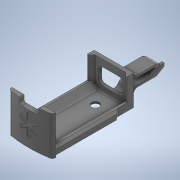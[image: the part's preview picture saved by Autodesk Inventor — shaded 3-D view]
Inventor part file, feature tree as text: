
AUTODESK INVENTOR PART (.ipt)
format: ipt  version: 2020 (Build 240168000, 168)  size: 811,008 bytes
history: native  units: mm
features: projected_geometry x32, extrude x18, sketch x16, fillet x10, other x9, chamfer x2
ambient origin geometry x8: Origin, YZ Plane, XZ Plane, XY Plane, X Axis, Y Axis, Z Axis, Center Point
bodies: Body1 (feature_tree)
feature tree (87):
  other  "Твердое тело1"
  sketch  "Эскиз1"
  extrude  "Выдавливание3"  Depth=202.0mm
  other  "РабПлоскость1"
  extrude  "Выдавливание1"  Depth=35.0mm
  other  "РабПлоскость2"
  sketch  "Эскиз2"
  extrude  "Выдавливание4"  Depth=68.0mm
  extrude  "Выдавливание5"  Depth=2.0mm
  sketch  "Эскиз4"
  extrude  "Выдавливание6"  Depth=2.0mm
  extrude  "Выдавливание7"  Depth=3.0mm
  other  "РабПлоскость3"
  extrude  "Выдавливание8"  Depth=3.0mm
  other  "РабПлоскость4"
  extrude  "Выдавливание9"  Depth=210.0mm
  sketch  "Эскиз8"
  extrude  "Выдавливание10"  Depth=20.0mm TaperAngle=0.0deg
  fillet  "Сопряжение1"  Radius=1.5mm
  fillet  "Сопряжение2"  Radius=28.0mm
  fillet  "Сопряжение3"  Radius=7.0mm
  fillet  "Сопряжение4"  Radius=20.0mm
  fillet  "Сопряжение5"  Radius=13.0mm
  extrude  "Выдавливание11"  Depth=5.0mm
  extrude  "Выдавливание12"  Depth=3.0mm
  fillet  "Сопряжение6"  Radius=10.0mm
  extrude  "Выдавливание13"  Depth=84.0mm
  chamfer  "Фаска1"  Distance=5.0mm
  fillet  "Сопряжение7"  Radius=52.0mm
  sketch  "Эскиз10"
  other  "РабПлоскость5"
  extrude  "Выдавливание14"  Depth=5.0mm TaperAngle=0.0deg
  fillet  "Сопряжение8"  Radius=35.0mm
  extrude  "Выдавливание15"  Depth=18.0mm
  fillet  "Сопряжение9"  Radius=3.0mm
  extrude  "Выдавливание16"  Depth=30.0mm TaperAngle=360.0deg
  fillet  "Сопряжение10"  Radius=0.5mm
  extrude  "Выдавливание17"  TaperAngle=0.0deg  [1 undecoded]
  chamfer  "Фаска2"  Distance=8.0mm
  other  "РабПлоскость10"
  other  "РабПлоскость9"
  sketch  "Эскиз14"
  other  "РабПлоскость8"
  sketch  "Эскиз15"
  sketch  "Эскиз16"
  sketch  "Эскиз17"
  extrude  "Выдавливание20"  Depth=2.0mm
  extrude  "Выдавливание21"  Depth=1.5mm TaperAngle=0.0deg
  projected_geometry  "Спроецированная петля1"
  projected_geometry  "Спроецированная петля7"
  projected_geometry  "Спроецированная петля8"
  sketch  "Эскиз3"
  projected_geometry  "Спроецированная петля9"
  projected_geometry  "Спроецированная петля10"
  projected_geometry  "Спроецированная петля11"
  projected_geometry  "Спроецированная петля12"
  sketch  "Эскиз5"
  projected_geometry  "Спроецированная петля13"
  projected_geometry  "Спроецированная петля14"
  projected_geometry  "Спроецированная петля15"
  projected_geometry  "Спроецированная петля16"
  projected_geometry  "Спроецированная петля17"
  sketch  "Эскиз6"
  projected_geometry  "Спроецированная петля18"
  projected_geometry  "Спроецированная петля19"
  projected_geometry  "Спроецированная петля20"
  projected_geometry  "Спроецированная петля21"
  projected_geometry  "Спроецированная петля22"
  projected_geometry  "Спроецированная петля23"
  projected_geometry  "Спроецированная петля24"
  projected_geometry  "Спроецированная петля25"
  projected_geometry  "Спроецированная петля26"
  projected_geometry  "Спроецированная петля27"
  projected_geometry  "Спроецированная петля28"
  sketch  "Эскиз9"
  projected_geometry  "Спроецированная петля29"
  projected_geometry  "Спроецированная петля30"
  sketch  "Эскиз11"
  projected_geometry  "Спроецированная петля31"
  projected_geometry  "Спроецированная петля32"
  projected_geometry  "Спроецированная петля33"
  sketch  "Эскиз12"
  projected_geometry  "Спроецированная петля34"
  projected_geometry  "Спроецированная петля35"
  projected_geometry  "Спроецированная петля37"
  sketch  "Эскиз18"
  projected_geometry  "Спроецированная петля38"
note: 1 required parameter value undecoded (feature->parameter linkage not recoverable at this tier; creation-order binding heuristic only, values carry confidence <= 0.55)
